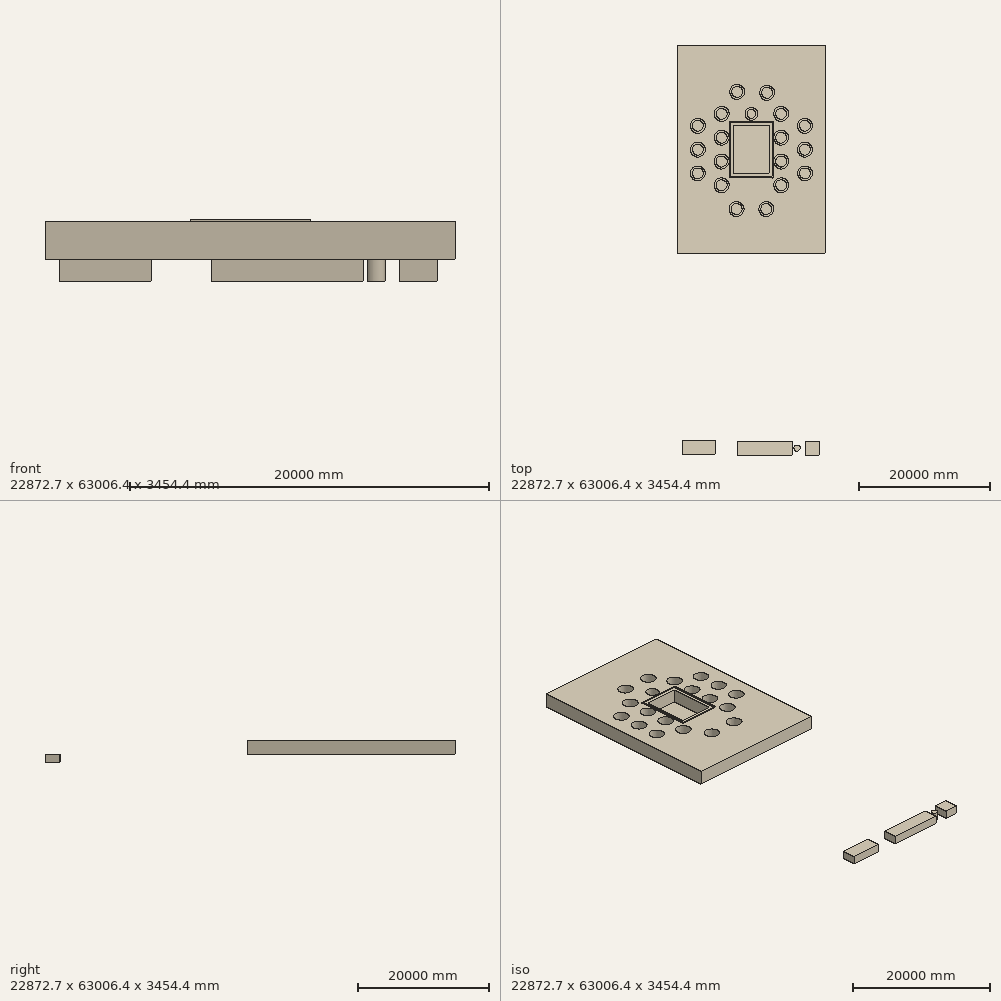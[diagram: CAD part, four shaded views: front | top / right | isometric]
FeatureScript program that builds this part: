
annotation { "Feature Type Name" : "Feature", "Feature Type Description" : "" }
export const myFeature = defineFeature(function(context is Context, id is Id, definition is map)
    precondition{}
    {
        {
            var Q0;
            Q0=qCreatedBy(makeId("Top.planeOp"),FACE);
            var sketch = newSketch(context, id + "F0", { "sketchPlane" : qUnion([Q0])});
            skLineSegment(sketch, "E0.bottom", {"start": v(0, 0) * mm, "end": v(22860, 0) * mm});
            skLineSegment(sketch, "E0.top", {"start": v(0, 32004) * mm, "end": v(22860, 32004) * mm});
            skLineSegment(sketch, "E0.left", {"start": v(0, 0) * mm, "end": v(0, 32004) * mm});
            skLineSegment(sketch, "E0.right", {"start": v(22860, 0) * mm, "end": v(22860, 32004) * mm});
            skSolve(sketch);
        }
        {
            var Q0;
            Q0=makeQuery(id+"F0.imprint","IMPRINT",FACE,{"disambiguationData":[TD([[makeQuery(id+"F0.imprint","IMPRINT",EDGE,{"derivedFrom":sQuery(id+"F0.wireOp",EDGE,"E0.bottom")}),1.0]])]});
            extrude(context, id + "F1", {"entities" : qUnion([Q0]), "offsetDistance" : 25.4 * mm, "depth" : 25.4 * mm});
        }
        {
            var Q0;
            Q0=qCreatedBy(makeId("Top.planeOp"),FACE);
            var sketch = newSketch(context, id + "F2", { "sketchPlane" : qUnion([Q0])});
            skLineSegment(sketch, "E1.bottom", {"start": v(0, 0) * mm, "end": v(22860, 0) * mm, "construction": true});
            skLineSegment(sketch, "E1.top", {"start": v(0, 32004) * mm, "end": v(22860, 32004) * mm, "construction": true});
            skLineSegment(sketch, "E1.left", {"start": v(0, 0) * mm, "end": v(0, 32004) * mm, "construction": true});
            skLineSegment(sketch, "E1.right", {"start": v(22860, 0) * mm, "end": v(22860, 32004) * mm, "construction": true});
            skCircle(sketch, "E2", {"center": v(9144, 6858) * mm, "radius": 838.2 * mm});
            skCircle(sketch, "E3", {"center": v(16002, 17830.8) * mm, "radius": 838.2 * mm});
            skCircle(sketch, "E4", {"center": v(16002, 10515.6) * mm, "radius": 838.2 * mm});
            skCircle(sketch, "E5", {"center": v(16002, 14173.2) * mm, "radius": 838.2 * mm});
            skCircle(sketch, "E6", {"center": v(16002, 21488.4) * mm, "radius": 838.2 * mm});
            skCircle(sketch, "E7", {"center": v(11430, 21488.4) * mm, "radius": 685.8 * mm});
            skCircle(sketch, "E8", {"center": v(13716, 6858) * mm, "radius": 838.2 * mm});
            skLineSegment(sketch, "E9.bottom", {"start": v(8686.8, 12344.4) * mm, "end": v(14173.2, 12344.4) * mm});
            skLineSegment(sketch, "E9.top", {"start": v(8686.8, 19659.6) * mm, "end": v(14173.2, 19659.6) * mm});
            skLineSegment(sketch, "E9.left", {"start": v(8686.8, 12344.4) * mm, "end": v(8686.8, 19659.6) * mm});
            skLineSegment(sketch, "E9.right", {"start": v(14173.2, 12344.4) * mm, "end": v(14173.2, 19659.6) * mm});
            skCircle(sketch, "E10", {"center": v(19659.6, 19659.6) * mm, "radius": 838.2 * mm});
            skLineSegment(sketch, "E11", {"start": v(0, 10515.6) * mm, "end": v(22860, 10515.6) * mm, "construction": true});
            skLineSegment(sketch, "E12", {"start": v(0, 21488.4) * mm, "end": v(22860, 21488.4) * mm, "construction": true});
            skPoint(sketch, "E13", {"position": v(22860, 16002) * mm});
            skPoint(sketch, "E14", {"position": v(14173.2, 16002) * mm});
            skLineSegment(sketch, "E15", {"start": v(14173.2, 16002) * mm, "end": v(22860, 16002) * mm, "construction": true});
            skPoint(sketch, "E16", {"position": v(11430, 12344.4) * mm});
            skPoint(sketch, "E17", {"position": v(11430, 0) * mm});
            skLineSegment(sketch, "E18", {"start": v(11430, 12344.4) * mm, "end": v(11430, 0) * mm, "construction": true});
            skLineSegment(sketch, "E19", {"start": v(16002, 32004) * mm, "end": v(16002, 0) * mm, "construction": true});
            skCircle(sketch, "E20", {"center": v(19659.6, 16002) * mm, "radius": 838.2 * mm});
            skCircle(sketch, "E21", {"center": v(19659.6, 12344.4) * mm, "radius": 838.2 * mm});
            skLineSegment(sketch, "E22", {"start": v(19659.6, 19659.6) * mm, "end": v(19659.6, 12344.4) * mm, "construction": true});
            skCircle(sketch, "E23.0", {"center": v(16002, 21488.4) * mm, "radius": 1143 * mm});
            skCircle(sketch, "E24.0", {"center": v(16002, 17830.8) * mm, "radius": 1143 * mm});
            skCircle(sketch, "E25.0", {"center": v(19659.6, 19659.6) * mm, "radius": 1143 * mm});
            skCircle(sketch, "E26.0", {"center": v(19659.6, 16002) * mm, "radius": 1143 * mm});
            skCircle(sketch, "E27.0", {"center": v(16002, 14173.2) * mm, "radius": 844.55 * mm});
            skCircle(sketch, "E28.0", {"center": v(16002, 14173.2) * mm, "radius": 1149.35 * mm});
            skCircle(sketch, "E29.0", {"center": v(19659.6, 12344.4) * mm, "radius": 1143 * mm});
            skCircle(sketch, "E30.0", {"center": v(16002, 10515.6) * mm, "radius": 1143 * mm});
            skCircle(sketch, "E31.MirrorC", {"center": v(6858, 10515.6) * mm, "radius": 1143 * mm});
            skCircle(sketch, "E32.MirrorC", {"center": v(6858, 10515.6) * mm, "radius": 838.2 * mm});
            skCircle(sketch, "E33.MirrorC", {"center": v(6858, 14173.2) * mm, "radius": 844.55 * mm});
            skCircle(sketch, "E34.MirrorC", {"center": v(6858, 14173.2) * mm, "radius": 1149.35 * mm});
            skCircle(sketch, "E35.MirrorC", {"center": v(3200.4, 12344.4) * mm, "radius": 1143 * mm});
            skCircle(sketch, "E36.MirrorC", {"center": v(3200.4, 12344.4) * mm, "radius": 838.2 * mm});
            skCircle(sketch, "E37.MirrorC", {"center": v(3200.4, 16002) * mm, "radius": 838.2 * mm});
            skCircle(sketch, "E38.MirrorC", {"center": v(3200.4, 16002) * mm, "radius": 1143 * mm});
            skCircle(sketch, "E39.MirrorC", {"center": v(6858, 17830.8) * mm, "radius": 838.2 * mm});
            skCircle(sketch, "E40.MirrorC", {"center": v(6858, 17830.8) * mm, "radius": 1143 * mm});
            skCircle(sketch, "E41.MirrorC", {"center": v(6858, 21488.4) * mm, "radius": 838.2 * mm});
            skCircle(sketch, "E42.MirrorC", {"center": v(6858, 21488.4) * mm, "radius": 1143 * mm});
            skCircle(sketch, "E43.MirrorC", {"center": v(3200.4, 19659.6) * mm, "radius": 838.2 * mm});
            skCircle(sketch, "E44.MirrorC", {"center": v(3200.4, 19659.6) * mm, "radius": 1143 * mm});
            skCircle(sketch, "E45", {"center": v(11430, 21488.4) * mm, "radius": 990.6 * mm});
            skLineSegment(sketch, "E46", {"start": v(9144, 6858) * mm, "end": v(13716, 6858) * mm, "construction": true});
            skCircle(sketch, "E47.0", {"center": v(9144, 6858) * mm, "radius": 1143 * mm});
            skCircle(sketch, "E48.0", {"center": v(13716, 6858) * mm, "radius": 844.55 * mm});
            skCircle(sketch, "E49.0", {"center": v(13716, 6858) * mm, "radius": 1143 * mm});
            skLineSegment(sketch, "E50.0", {"start": v(-6.35, 32010.35) * mm, "end": v(22866.35, 32010.35) * mm});
            skLineSegment(sketch, "E50.1", {"start": v(22866.35, 32010.35) * mm, "end": v(22866.35, -6.35) * mm});
            skLineSegment(sketch, "E50.2", {"start": v(22866.35, -6.35) * mm, "end": v(-6.35, -6.35) * mm});
            skLineSegment(sketch, "E50.3", {"start": v(-6.35, -6.35) * mm, "end": v(-6.35, 32010.35) * mm});
            skLineSegment(sketch, "E51.0", {"start": v(8077.2, 11734.8) * mm, "end": v(8077.2, 20269.2) * mm, "construction": true});
            skLineSegment(sketch, "E51.1", {"start": v(8077.2, 11734.8) * mm, "end": v(14782.8, 11734.8) * mm, "construction": true});
            skCircle(sketch, "E52", {"center": v(8077.2, 11734.8) * mm, "radius": 101.6 * mm});
            skCircle(sketch, "E53.MirrorC", {"center": v(14782.8, 11734.8) * mm, "radius": 101.6 * mm});
            skCircle(sketch, "E54.MirrorC", {"center": v(8077.2, 20269.2) * mm, "radius": 101.6 * mm});
            skCircle(sketch, "E55.MirrorC", {"center": v(14782.8, 20269.2) * mm, "radius": 101.6 * mm});
            skCircle(sketch, "E56.MirrorC", {"center": v(9253.47, 24868.12) * mm, "radius": 838.2 * mm});
            skCircle(sketch, "E57.MirrorC", {"center": v(9253.47, 24868.12) * mm, "radius": 1143 * mm});
            skCircle(sketch, "E58.MirrorC", {"center": v(13846.17, 24722.43) * mm, "radius": 838.2 * mm});
            skCircle(sketch, "E59.MirrorC", {"center": v(13846.17, 24722.43) * mm, "radius": 1143 * mm});
            skSolve(sketch);
        }
        {
            var Q0;
            Q0=makeQuery(id+"F2.imprint","IMPRINT",FACE,{"disambiguationData":[TD([[makeQuery(id+"F2.imprint","IMPRINT",EDGE,{"derivedFrom":sQuery(id+"F2.wireOp",EDGE,"E9.bottom")}),1.0]])]});
            var Q1;
            Q1=sQuery(id+"F2.wireOp",EDGE,"E9.left");
            var Q2;
            Q2=sQuery(id+"F2.wireOp",EDGE,"E9.top");
            var Q3;
            Q3=sQuery(id+"F2.wireOp",EDGE,"E9.right");
            var Q4;
            Q4=sQuery(id+"F2.wireOp",EDGE,"E9.bottom");
            extrude(context, id + "F3", {"entities" : qUnion([Q0]), "surfaceEntities" : qUnion([Q1, Q2, Q3, Q4]), "depth" : 76.2 * mm});
        }
        {
            var Q0;
            Q0=makeQuery(id+"F2.imprint","IMPRINT",FACE,{"disambiguationData":[TD([[makeQuery(id+"F2.imprint","IMPRINT",EDGE,{"derivedFrom":sQuery(id+"F2.wireOp",EDGE,"E36.MirrorC")}),-1.0]])]});
            var Q1;
            Q1=makeQuery(id+"F2.imprint","IMPRINT",FACE,{"disambiguationData":[TD([[makeQuery(id+"F2.imprint","IMPRINT",EDGE,{"derivedFrom":sQuery(id+"F2.wireOp",EDGE,"E37.MirrorC")}),-1.0]])]});
            var Q2;
            Q2=makeQuery(id+"F2.imprint","IMPRINT",FACE,{"disambiguationData":[TD([[makeQuery(id+"F2.imprint","IMPRINT",EDGE,{"derivedFrom":sQuery(id+"F2.wireOp",EDGE,"E43.MirrorC")}),-1.0]])]});
            var Q3;
            Q3=makeQuery(id+"F2.imprint","IMPRINT",FACE,{"disambiguationData":[TD([[makeQuery(id+"F2.imprint","IMPRINT",EDGE,{"derivedFrom":sQuery(id+"F2.wireOp",EDGE,"E41.MirrorC")}),-1.0]])]});
            var Q4;
            Q4=makeQuery(id+"F2.imprint","IMPRINT",FACE,{"disambiguationData":[TD([[makeQuery(id+"F2.imprint","IMPRINT",EDGE,{"derivedFrom":sQuery(id+"F2.wireOp",EDGE,"296d55f4-9c03-4749-9ef3-5b14feb4dc1d0.MirrorC")}),-1.0]])]});
            var Q5;
            Q5=makeQuery(id+"F2.imprint","IMPRINT",FACE,{"disambiguationData":[TD([[makeQuery(id+"F2.imprint","IMPRINT",EDGE,{"derivedFrom":sQuery(id+"F2.wireOp",EDGE,"93b23867-7506-4d4e-b67f-f578fab0a0a10.MirrorC")}),-1.0]])]});
            var Q6;
            Q6=makeQuery(id+"F2.imprint","IMPRINT",FACE,{"disambiguationData":[TD([[makeQuery(id+"F2.imprint","IMPRINT",EDGE,{"derivedFrom":sQuery(id+"F2.wireOp",EDGE,"E7")}),1.0]])]});
            var Q7;
            Q7=makeQuery(id+"F2.imprint","IMPRINT",FACE,{"disambiguationData":[TD([[makeQuery(id+"F2.imprint","IMPRINT",EDGE,{"derivedFrom":sQuery(id+"F2.wireOp",EDGE,"6e906669-6044-44f8-b0b6-e3eeb8bcd6010.MirrorC")}),-1.0]])]});
            var Q8;
            Q8=makeQuery(id+"F2.imprint","IMPRINT",FACE,{"disambiguationData":[TD([[makeQuery(id+"F2.imprint","IMPRINT",EDGE,{"derivedFrom":sQuery(id+"F2.wireOp",EDGE,"E6")}),1.0]])]});
            var Q9;
            Q9=makeQuery(id+"F2.imprint","IMPRINT",FACE,{"disambiguationData":[TD([[makeQuery(id+"F2.imprint","IMPRINT",EDGE,{"derivedFrom":sQuery(id+"F2.wireOp",EDGE,"E10")}),1.0]])]});
            var Q10;
            Q10=makeQuery(id+"F2.imprint","IMPRINT",FACE,{"disambiguationData":[TD([[makeQuery(id+"F2.imprint","IMPRINT",EDGE,{"derivedFrom":sQuery(id+"F2.wireOp",EDGE,"E20")}),1.0]])]});
            var Q11;
            Q11=makeQuery(id+"F2.imprint","IMPRINT",FACE,{"disambiguationData":[TD([[makeQuery(id+"F2.imprint","IMPRINT",EDGE,{"derivedFrom":sQuery(id+"F2.wireOp",EDGE,"E3")}),1.0]])]});
            var Q12;
            Q12=makeQuery(id+"F2.imprint","IMPRINT",FACE,{"disambiguationData":[TD([[makeQuery(id+"F2.imprint","IMPRINT",EDGE,{"derivedFrom":sQuery(id+"F2.wireOp",EDGE,"E5")}),1.0]])]});
            var Q13;
            Q13=makeQuery(id+"F2.imprint","IMPRINT",FACE,{"disambiguationData":[TD([[makeQuery(id+"F2.imprint","IMPRINT",EDGE,{"derivedFrom":sQuery(id+"F2.wireOp",EDGE,"E21")}),1.0]])]});
            var Q14;
            Q14=makeQuery(id+"F2.imprint","IMPRINT",FACE,{"disambiguationData":[TD([[makeQuery(id+"F2.imprint","IMPRINT",EDGE,{"derivedFrom":sQuery(id+"F2.wireOp",EDGE,"E4")}),1.0]])]});
            var Q15;
            Q15=makeQuery(id+"F2.imprint","IMPRINT",FACE,{"disambiguationData":[TD([[makeQuery(id+"F2.imprint","IMPRINT",EDGE,{"derivedFrom":sQuery(id+"F2.wireOp",EDGE,"db3ed8bb-662f-4947-82cb-c84062fed37e")}),1.0]])]});
            var Q16;
            Q16=makeQuery(id+"F2.imprint","IMPRINT",FACE,{"disambiguationData":[TD([[makeQuery(id+"F2.imprint","IMPRINT",EDGE,{"derivedFrom":sQuery(id+"F2.wireOp",EDGE,"E8")}),1.0]])]});
            var Q17;
            Q17=makeQuery(id+"F2.imprint","IMPRINT",FACE,{"disambiguationData":[TD([[makeQuery(id+"F2.imprint","IMPRINT",EDGE,{"derivedFrom":sQuery(id+"F2.wireOp",EDGE,"8d3556f3-34ba-4986-b1d8-e773021c0981")}),1.0]])]});
            var Q18;
            Q18=makeQuery(id+"F2.imprint","IMPRINT",FACE,{"disambiguationData":[TD([[makeQuery(id+"F2.imprint","IMPRINT",EDGE,{"derivedFrom":sQuery(id+"F2.wireOp",EDGE,"E2")}),1.0]])]});
            var Q19;
            Q19=makeQuery(id+"F2.imprint","IMPRINT",FACE,{"disambiguationData":[TD([[makeQuery(id+"F2.imprint","IMPRINT",EDGE,{"derivedFrom":sQuery(id+"F2.wireOp",EDGE,"E32.MirrorC")}),-1.0]])]});
            var Q20;
            Q20=makeQuery(id+"F2.imprint","IMPRINT",FACE,{"disambiguationData":[TD([[makeQuery(id+"F2.imprint","IMPRINT",EDGE,{"derivedFrom":sQuery(id+"F2.wireOp",EDGE,"E33.MirrorC")}),-1.0]])]});
            var Q21;
            Q21=makeQuery(id+"F2.imprint","IMPRINT",FACE,{"disambiguationData":[TD([[makeQuery(id+"F2.imprint","IMPRINT",EDGE,{"derivedFrom":sQuery(id+"F2.wireOp",EDGE,"E39.MirrorC")}),-1.0]])]});
            var Q22;
            Q22=makeQuery(id+"F2.imprint","IMPRINT",FACE,{"disambiguationData":[TD([[makeQuery(id+"F2.imprint","IMPRINT",EDGE,{"derivedFrom":sQuery(id+"F2.wireOp",EDGE,"E56.MirrorC")}),-1.0]])]});
            var Q23;
            Q23=makeQuery(id+"F2.imprint","IMPRINT",FACE,{"disambiguationData":[TD([[makeQuery(id+"F2.imprint","IMPRINT",EDGE,{"derivedFrom":sQuery(id+"F2.wireOp",EDGE,"FGtwzOV2-lLvm-BpAb-7a3C-8KjCMGtIFXAM")}),1.0]])]});
            var Q24;
            Q24=makeQuery(id+"F2.imprint","IMPRINT",FACE,{"disambiguationData":[TD([[makeQuery(id+"F2.imprint","IMPRINT",EDGE,{"derivedFrom":sQuery(id+"F2.wireOp",EDGE,"E58.MirrorC")}),-1.0]])]});
            var Q25;
            Q25=makeQuery(id+"F2.imprint","IMPRINT",FACE,{"disambiguationData":[TD([[makeQuery(id+"F2.imprint","IMPRINT",EDGE,{"derivedFrom":sQuery(id+"F2.wireOp",EDGE,"E9.bottom")}),-1.0]])]});
            var Q26;
            Q26=sQuery(id+"F2.wireOp",EDGE,"E36.MirrorC");
            var Q27;
            Q27=sQuery(id+"F2.wireOp",EDGE,"E37.MirrorC");
            var Q28;
            Q28=sQuery(id+"F2.wireOp",EDGE,"E43.MirrorC");
            var Q29;
            Q29=sQuery(id+"F2.wireOp",EDGE,"E41.MirrorC");
            var Q30;
            Q30=sQuery(id+"F2.wireOp",EDGE,"296d55f4-9c03-4749-9ef3-5b14feb4dc1d0.MirrorC");
            var Q31;
            Q31=sQuery(id+"F2.wireOp",EDGE,"93b23867-7506-4d4e-b67f-f578fab0a0a10.MirrorC");
            var Q32;
            Q32=sQuery(id+"F2.wireOp",EDGE,"6e906669-6044-44f8-b0b6-e3eeb8bcd6010.MirrorC");
            var Q33;
            Q33=sQuery(id+"F2.wireOp",EDGE,"E39.MirrorC");
            var Q34;
            Q34=sQuery(id+"F2.wireOp",EDGE,"E33.MirrorC");
            var Q35;
            Q35=sQuery(id+"F2.wireOp",EDGE,"E32.MirrorC");
            var Q36;
            Q36=sQuery(id+"F2.wireOp",EDGE,"E2");
            var Q37;
            Q37=sQuery(id+"F2.wireOp",EDGE,"8d3556f3-34ba-4986-b1d8-e773021c0981");
            var Q38;
            Q38=sQuery(id+"F2.wireOp",EDGE,"db3ed8bb-662f-4947-82cb-c84062fed37e");
            var Q39;
            Q39=sQuery(id+"F2.wireOp",EDGE,"E8");
            var Q40;
            Q40=sQuery(id+"F2.wireOp",EDGE,"E4");
            var Q41;
            Q41=sQuery(id+"F2.wireOp",EDGE,"E5");
            var Q42;
            Q42=sQuery(id+"F2.wireOp",EDGE,"E3");
            var Q43;
            Q43=sQuery(id+"F2.wireOp",EDGE,"E7");
            var Q44;
            Q44=sQuery(id+"F2.wireOp",EDGE,"E6");
            var Q45;
            Q45=sQuery(id+"F2.wireOp",EDGE,"E10");
            var Q46;
            Q46=sQuery(id+"F2.wireOp",EDGE,"E20");
            var Q47;
            Q47=sQuery(id+"F2.wireOp",EDGE,"E21");
            extrude(context, id + "F4", {"entities" : qUnion([Q0, Q1, Q2, Q3, Q4, Q5, Q6, Q7, Q8, Q9, Q10, Q11, Q12, Q13, Q14, Q15, Q16, Q17, Q18, Q19, Q20, Q21, Q22, Q23, Q24, Q25]), "surfaceEntities" : qUnion([Q26, Q27, Q28, Q29, Q30, Q31, Q32, Q33, Q34, Q35, Q36, Q37, Q38, Q39, Q40, Q41, Q42, Q43, Q44, Q45, Q46, Q47]), "offsetDistance" : 25.4 * mm, "depth" : 685.8 * mm});
        }
        {
            var Q0;
            Q0=makeQuery(id+"F2.imprint","IMPRINT",FACE,{"disambiguationData":[TD([[makeQuery(id+"F2.imprint","IMPRINT",EDGE,{"derivedFrom":sQuery(id+"F2.wireOp",EDGE,"8d3556f3-34ba-4986-b1d8-e773021c0981")}),-1.0]])]});
            var Q1;
            Q1=makeQuery(id+"F2.imprint","IMPRINT",FACE,{"disambiguationData":[TD([[makeQuery(id+"F2.imprint","IMPRINT",EDGE,{"derivedFrom":sQuery(id+"F2.wireOp",EDGE,"E2")}),-1.0]])]});
            var Q2;
            Q2=makeQuery(id+"F2.imprint","IMPRINT",FACE,{"disambiguationData":[TD([[makeQuery(id+"F2.imprint","IMPRINT",EDGE,{"derivedFrom":sQuery(id+"F2.wireOp",EDGE,"E31.MirrorC")}),-1.0]])]});
            var Q3;
            Q3=makeQuery(id+"F2.imprint","IMPRINT",FACE,{"disambiguationData":[TD([[makeQuery(id+"F2.imprint","IMPRINT",EDGE,{"derivedFrom":sQuery(id+"F2.wireOp",EDGE,"E35.MirrorC")}),-1.0]])]});
            var Q4;
            Q4=makeQuery(id+"F2.imprint","IMPRINT",FACE,{"disambiguationData":[TD([[makeQuery(id+"F2.imprint","IMPRINT",EDGE,{"derivedFrom":sQuery(id+"F2.wireOp",EDGE,"E37.MirrorC")}),1.0]])]});
            var Q5;
            Q5=makeQuery(id+"F2.imprint","IMPRINT",FACE,{"disambiguationData":[TD([[makeQuery(id+"F2.imprint","IMPRINT",EDGE,{"derivedFrom":sQuery(id+"F2.wireOp",EDGE,"E43.MirrorC")}),1.0]])]});
            var Q6;
            Q6=makeQuery(id+"F2.imprint","IMPRINT",FACE,{"disambiguationData":[TD([[makeQuery(id+"F2.imprint","IMPRINT",EDGE,{"derivedFrom":sQuery(id+"F2.wireOp",EDGE,"E41.MirrorC")}),1.0]])]});
            var Q7;
            Q7=makeQuery(id+"F2.imprint","IMPRINT",FACE,{"disambiguationData":[TD([[makeQuery(id+"F2.imprint","IMPRINT",EDGE,{"derivedFrom":sQuery(id+"F2.wireOp",EDGE,"296d55f4-9c03-4749-9ef3-5b14feb4dc1d0.MirrorC")}),1.0]])]});
            var Q8;
            Q8=makeQuery(id+"F2.imprint","IMPRINT",FACE,{"disambiguationData":[TD([[makeQuery(id+"F2.imprint","IMPRINT",EDGE,{"derivedFrom":sQuery(id+"F2.wireOp",EDGE,"E7")}),-1.0]])]});
            var Q9;
            Q9=makeQuery(id+"F2.imprint","IMPRINT",FACE,{"disambiguationData":[TD([[makeQuery(id+"F2.imprint","IMPRINT",EDGE,{"derivedFrom":sQuery(id+"F2.wireOp",EDGE,"93b23867-7506-4d4e-b67f-f578fab0a0a10.MirrorC")}),1.0]])]});
            var Q10;
            Q10=makeQuery(id+"F2.imprint","IMPRINT",FACE,{"disambiguationData":[TD([[makeQuery(id+"F2.imprint","IMPRINT",EDGE,{"derivedFrom":sQuery(id+"F2.wireOp",EDGE,"6e906669-6044-44f8-b0b6-e3eeb8bcd6010.MirrorC")}),1.0]])]});
            var Q11;
            Q11=makeQuery(id+"F2.imprint","IMPRINT",FACE,{"disambiguationData":[TD([[makeQuery(id+"F2.imprint","IMPRINT",EDGE,{"derivedFrom":sQuery(id+"F2.wireOp",EDGE,"E6")}),-1.0]])]});
            var Q12;
            Q12=makeQuery(id+"F2.imprint","IMPRINT",FACE,{"disambiguationData":[TD([[makeQuery(id+"F2.imprint","IMPRINT",EDGE,{"derivedFrom":sQuery(id+"F2.wireOp",EDGE,"E3")}),-1.0]])]});
            var Q13;
            Q13=makeQuery(id+"F2.imprint","IMPRINT",FACE,{"disambiguationData":[TD([[makeQuery(id+"F2.imprint","IMPRINT",EDGE,{"derivedFrom":sQuery(id+"F2.wireOp",EDGE,"E10")}),-1.0]])]});
            var Q14;
            Q14=makeQuery(id+"F2.imprint","IMPRINT",FACE,{"disambiguationData":[TD([[makeQuery(id+"F2.imprint","IMPRINT",EDGE,{"derivedFrom":sQuery(id+"F2.wireOp",EDGE,"E27.0")}),-1.0]])]});
            var Q15;
            Q15=makeQuery(id+"F2.imprint","IMPRINT",FACE,{"disambiguationData":[TD([[makeQuery(id+"F2.imprint","IMPRINT",EDGE,{"derivedFrom":sQuery(id+"F2.wireOp",EDGE,"E20")}),-1.0]])]});
            var Q16;
            Q16=makeQuery(id+"F2.imprint","IMPRINT",FACE,{"disambiguationData":[TD([[makeQuery(id+"F2.imprint","IMPRINT",EDGE,{"derivedFrom":sQuery(id+"F2.wireOp",EDGE,"E21")}),-1.0]])]});
            var Q17;
            Q17=makeQuery(id+"F2.imprint","IMPRINT",FACE,{"disambiguationData":[TD([[makeQuery(id+"F2.imprint","IMPRINT",EDGE,{"derivedFrom":sQuery(id+"F2.wireOp",EDGE,"E4")}),-1.0]])]});
            var Q18;
            Q18=makeQuery(id+"F2.imprint","IMPRINT",FACE,{"disambiguationData":[TD([[makeQuery(id+"F2.imprint","IMPRINT",EDGE,{"derivedFrom":sQuery(id+"F2.wireOp",EDGE,"db3ed8bb-662f-4947-82cb-c84062fed37e")}),-1.0]])]});
            var Q19;
            Q19=makeQuery(id+"F2.imprint","IMPRINT",FACE,{"disambiguationData":[TD([[makeQuery(id+"F2.imprint","IMPRINT",EDGE,{"derivedFrom":sQuery(id+"F2.wireOp",EDGE,"E48.0")}),-1.0]])]});
            var Q20;
            Q20=makeQuery(id+"F2.imprint","IMPRINT",FACE,{"disambiguationData":[TD([[makeQuery(id+"F2.imprint","IMPRINT",EDGE,{"derivedFrom":sQuery(id+"F2.wireOp",EDGE,"E33.MirrorC")}),1.0]])]});
            var Q21;
            Q21=makeQuery(id+"F2.imprint","IMPRINT",FACE,{"disambiguationData":[TD([[makeQuery(id+"F2.imprint","IMPRINT",EDGE,{"derivedFrom":sQuery(id+"F2.wireOp",EDGE,"E39.MirrorC")}),1.0]])]});
            extrude(context, id + "F5", {"entities" : qUnion([Q0, Q1, Q2, Q3, Q4, Q5, Q6, Q7, Q8, Q9, Q10, Q11, Q12, Q13, Q14, Q15, Q16, Q17, Q18, Q19, Q20, Q21]), "depth" : 355.6 * mm});
        }
        {
            var Q0;
            Q0=makeQuery(id+"F2.imprint","IMPRINT",FACE,{"disambiguationData":[TD([[makeQuery(id+"F2.imprint","IMPRINT",EDGE,{"derivedFrom":sQuery(id+"F2.wireOp",EDGE,"E54.MirrorC")}),-1.0]])]});
            var Q1;
            Q1=makeQuery(id+"F2.imprint","IMPRINT",FACE,{"disambiguationData":[TD([[makeQuery(id+"F2.imprint","IMPRINT",EDGE,{"derivedFrom":sQuery(id+"F2.wireOp",EDGE,"E55.MirrorC")}),1.0]])]});
            var Q2;
            Q2=makeQuery(id+"F2.imprint","IMPRINT",FACE,{"disambiguationData":[TD([[makeQuery(id+"F2.imprint","IMPRINT",EDGE,{"derivedFrom":sQuery(id+"F2.wireOp",EDGE,"E52")}),1.0]])]});
            var Q3;
            Q3=makeQuery(id+"F2.imprint","IMPRINT",FACE,{"disambiguationData":[TD([[makeQuery(id+"F2.imprint","IMPRINT",EDGE,{"derivedFrom":sQuery(id+"F2.wireOp",EDGE,"E53.MirrorC")}),-1.0]])]});
            extrude(context, id + "F6", {"entities" : qUnion([Q0, Q1, Q2, Q3]), "operationType" : NewBodyOperationType.ADD, "depth" : 2133.6 * mm});
        }
        {
            var Q0;
            Q0=makeQuery(id+"F6.opExtrude","CAP_FACE",FACE,{"disambiguationData":[OSD([sQuery(id+"F2.wireOp",EDGE,"E53.MirrorC")])],"isStart":false});
            cPlane(context, id + "F7", {"entities" : qUnion([Q0]), "cplaneType" : CPlaneType.OFFSET, "offset" : 0 * mm, "width" : 152.4 * mm, "height" : 152.4 * mm});
        }
        {
            var Q0;
            Q0=qCreatedBy(id+"F7.planeOp",FACE);
            var sketch = newSketch(context, id + "F8", { "sketchPlane" : qUnion([Q0])});
            skLineSegment(sketch, "E60.bottom", {"start": v(14782.8, 11734.8) * mm, "end": v(8077.2, 11734.8) * mm});
            skLineSegment(sketch, "E60.top", {"start": v(14782.8, 20269.2) * mm, "end": v(8077.2, 20269.2) * mm});
            skLineSegment(sketch, "E60.left", {"start": v(14782.8, 11734.8) * mm, "end": v(14782.8, 20269.2) * mm});
            skLineSegment(sketch, "E60.right", {"start": v(8077.2, 11734.8) * mm, "end": v(8077.2, 20269.2) * mm});
            skLineSegment(sketch, "E61.0", {"start": v(14681.2, 11836.4) * mm, "end": v(8178.8, 11836.4) * mm});
            skLineSegment(sketch, "E61.1", {"start": v(14681.2, 11836.4) * mm, "end": v(14681.2, 20167.6) * mm});
            skLineSegment(sketch, "E61.2", {"start": v(14681.2, 20167.6) * mm, "end": v(8178.8, 20167.6) * mm});
            skLineSegment(sketch, "E61.3", {"start": v(8178.8, 11836.4) * mm, "end": v(8178.8, 20167.6) * mm});
            skSolve(sketch);
        }
        {
            var Q0;
            Q0 = qSketchRegion(id + "F8", true);
            extrude(context, id + "F9", {"entities" : qUnion([Q0]), "operationType" : NewBodyOperationType.ADD, "depth" : 101.6 * mm});
        }
        {
            var Q0;
            Q0=makeQuery(id+"F1.opExtrude","CAP_FACE",FACE,{"disambiguationData":[OSD([sQuery(id+"F0.wireOp",EDGE,"E0.bottom"),sQuery(id+"F0.wireOp",EDGE,"E0.top"),sQuery(id+"F0.wireOp",EDGE,"E0.left"),sQuery(id+"F0.wireOp",EDGE,"E0.right")])],"isStart":true});
            var sketch = newSketch(context, id + "F10", { "sketchPlane" : qUnion([Q0])});
            skLineSegment(sketch, "E62.bottom", {"start": v(790.3, 30871.7) * mm, "end": v(5908.52, 30871.7) * mm});
            skLineSegment(sketch, "E62.top", {"start": v(790.3, 28688.8) * mm, "end": v(5908.52, 28688.8) * mm});
            skLineSegment(sketch, "E62.left", {"start": v(790.3, 30871.7) * mm, "end": v(790.3, 28688.8) * mm});
            skLineSegment(sketch, "E62.right", {"start": v(5908.52, 30871.7) * mm, "end": v(5908.52, 28688.8) * mm});
            skLineSegment(sketch, "E63.bottom", {"start": v(9244.46, 30996.02) * mm, "end": v(17711.52, 30996.02) * mm});
            skLineSegment(sketch, "E63.top", {"start": v(9244.46, 28787.22) * mm, "end": v(17711.52, 28787.22) * mm});
            skLineSegment(sketch, "E63.left", {"start": v(9244.46, 30996.02) * mm, "end": v(9244.46, 28787.22) * mm});
            skLineSegment(sketch, "E63.right", {"start": v(17711.52, 30996.02) * mm, "end": v(17711.52, 28787.22) * mm});
            skLineSegment(sketch, "E64.bottom", {"start": v(19736.26, 30996.02) * mm, "end": v(21883.7, 30996.02) * mm});
            skLineSegment(sketch, "E64.top", {"start": v(19736.26, 28787.22) * mm, "end": v(21883.7, 28787.22) * mm});
            skLineSegment(sketch, "E64.left", {"start": v(19736.26, 30996.02) * mm, "end": v(19736.26, 28787.22) * mm});
            skLineSegment(sketch, "E64.right", {"start": v(21883.7, 30996.02) * mm, "end": v(21883.7, 28787.22) * mm});
            skCircle(sketch, "E65", {"center": v(18447.8, 29891.62) * mm, "radius": 490.84 * mm});
            skSolve(sketch);
        }
        {
            var Q0;
            Q0 = qSketchRegion(id + "F10", true);
            extrude(context, id + "F11", {"entities" : qUnion([Q0]), "operationType" : NewBodyOperationType.ADD, "depth" : 1219.2 * mm, "offsetDistance" : 25.4 * mm});
        }
    });
